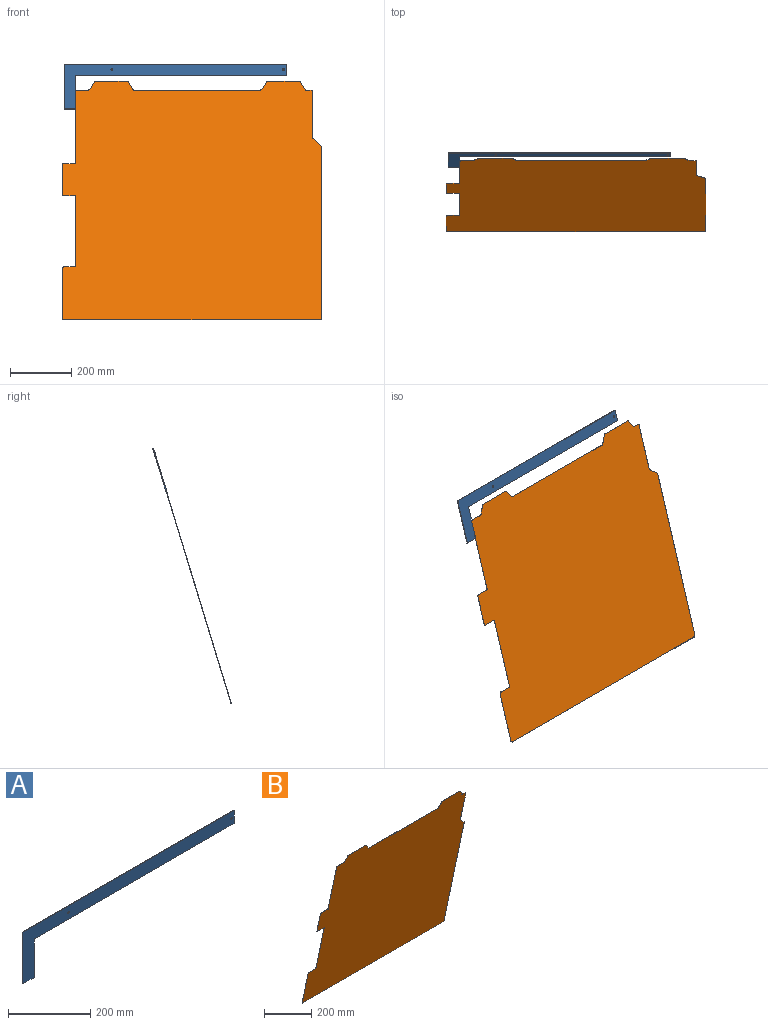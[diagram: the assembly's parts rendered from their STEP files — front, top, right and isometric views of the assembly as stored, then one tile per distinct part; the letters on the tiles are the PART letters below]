
ASSEMBLY  parts=2 mates=1
PART A: 10 faces, bbox 723.9x3.2x152.4 mm
  f0: plane 38.1x3.18mm, normal (1,0,0), area 121mm2, adj f1,f7,f8,f9
  f1: plane 723.9x3.18mm, normal (0,0,1), area 2298.4mm2, adj f0,f2,f8,f9
  f2: plane 152.4x3.18mm, normal (-1,0,0), area 483.9mm2, adj f1,f3,f8,f9
  f3: plane 38.1x3.18mm, normal (0,0,-1), area 121mm2, adj f2,f4,f8,f9
  f4: plane 114.3x3.18mm, normal (1,0,0), area 362.9mm2, adj f3,f7,f8,f9
  f5: cylinder r=3.17mm len=6.35mm, axis (0,1,0), area 63.3mm2, adj f8,f9
  f6: cylinder r=3.17mm len=6.35mm, axis (0,1,0), area 63.3mm2, adj f8,f9
  f7: plane 685.8x3.18mm, normal (0,0,-1), area 2177.4mm2, adj f0,f4,f8,f9
  f8: plane 723.9x152.4mm, normal (0,-1,0), area 31872.1mm2, adj f0,f1,f2,f3,f4,f5,f6,f7
  f9: plane 723.9x152.4mm, normal (0,1,0), area 31872.1mm2, adj f0,f1,f2,f3,f4,f5,f6,f7
PART B: 42 faces, bbox 845.6x169.3x794.4 mm
  f0: plane 845.62x794.26mm, normal (0,0.98,0.21), area 641403.5mm2, adj f1,f2,f3,f4,f5,f6,f7,f8
  f1: cylinder r=1mm len=1.08mm, axis (0,0.98,0.21), area 0.8mm2, adj f0,f2,f40,f41
  f2: plane 38.7x0.5mm, normal (0,0.21,-0.98), area 19.7mm2, adj f0,f1,f3,f41
  f3: cylinder r=5mm len=5mm, axis (0,0.98,0.21), area 4mm2, adj f0,f2,f4,f41
  f4: plane 97.82x21.27mm, normal (-1,0,0), area 50.7mm2, adj f0,f3,f5,f41
  f5: cylinder r=5mm len=5mm, axis (0,0.98,0.21), area 4mm2, adj f0,f4,f6,f41
  f6: plane 38.7x0.5mm, normal (0,-0.21,0.98), area 19.7mm2, adj f0,f5,f7,f41
  f7: cylinder r=1mm len=1.08mm, axis (0,0.98,0.21), area 0.8mm2, adj f0,f6,f8,f41
  f8: plane 239.07x51.29mm, normal (-1,0,0), area 124.1mm2, adj f0,f7,f9,f41
  f9: cylinder r=5mm len=5mm, axis (0,0.98,0.21), area 4mm2, adj f0,f8,f10,f41
  f10: plane 36.06x0.5mm, normal (0,-0.21,0.98), area 18.3mm2, adj f0,f9,f11,f41
  f11: cylinder r=5mm len=4.33mm, axis (0,0.98,0.21), area 2.7mm2, adj f0,f10,f12,f41
  f12: plane 24.56x14.43mm, normal (-0.87,-0.1,0.49), area 14.7mm2, adj f0,f11,f13,f41
  f13: cylinder r=5mm len=4.33mm, axis (0,0.98,0.21), area 2.7mm2, adj f0,f12,f14,f41
  f14: plane 103.09x0.5mm, normal (0,-0.21,0.98), area 52.4mm2, adj f0,f13,f15,f41
  f15: cylinder r=5mm len=4.33mm, axis (0,0.98,0.21), area 2.7mm2, adj f0,f14,f16,f41
  f16: plane 24.56x14.43mm, normal (0.87,-0.1,0.49), area 14.7mm2, adj f0,f15,f17,f41
  f17: cylinder r=5mm len=4.33mm, axis (0,0.98,0.21), area 2.7mm2, adj f0,f16,f18,f41
  f18: plane 410.72x0.5mm, normal (0,-0.21,0.98), area 208.6mm2, adj f0,f17,f19,f41
  f19: cylinder r=5mm len=4.33mm, axis (0,0.98,0.21), area 2.7mm2, adj f0,f18,f20,f41
  f20: plane 24.56x14.43mm, normal (-0.87,-0.1,0.49), area 14.7mm2, adj f0,f19,f21,f41
  f21: cylinder r=5mm len=4.33mm, axis (0,0.98,0.21), area 2.7mm2, adj f0,f20,f22,f41
  f22: plane 103.09x0.5mm, normal (0,-0.21,0.98), area 52.4mm2, adj f0,f21,f23,f41
  f23: cylinder r=5mm len=4.33mm, axis (0,0.98,0.21), area 2.7mm2, adj f0,f22,f24,f41
  f24: plane 24.56x14.43mm, normal (0.87,-0.1,0.49), area 14.7mm2, adj f0,f23,f25,f41
  f25: cylinder r=5mm len=4.33mm, axis (0,0.98,0.21), area 2.7mm2, adj f0,f24,f26,f41
  f26: plane 15.36x0.5mm, normal (0,-0.21,0.98), area 7.8mm2, adj f0,f25,f27,f41
  f27: cylinder r=5mm len=5mm, axis (0,0.98,0.21), area 4mm2, adj f0,f26,f28,f41
  f28: plane 153.67x33.14mm, normal (1,0,0), area 79.8mm2, adj f0,f27,f29,f41
  f29: cylinder r=5mm len=3.56mm, axis (0,0.98,0.21), area 2mm2, adj f0,f28,f30,f41
  f30: plane 27.29x26.8mm, normal (0.71,-0.15,0.69), area 19.6mm2, adj f0,f29,f31,f41
  f31: cylinder r=5mm len=3.56mm, axis (0,0.98,0.21), area 2mm2, adj f0,f30,f32,f41
  f32: plane 568.06x121.22mm, normal (1,0,0), area 295mm2, adj f0,f31,f33,f41
  f33: cylinder r=5mm len=5mm, axis (0,0.98,0.21), area 4mm2, adj f0,f32,f34,f41
  f34: plane 835.62x0.5mm, normal (0,0.21,-0.98), area 424.5mm2, adj f0,f33,f35,f41
  f35: cylinder r=5mm len=5mm, axis (0,0.98,0.21), area 4mm2, adj f0,f34,f36,f41
  f36: plane 166.59x35.88mm, normal (-1,0,0), area 86.5mm2, adj f0,f35,f37,f41
  f37: cylinder r=5mm len=5mm, axis (0,0.98,0.21), area 4mm2, adj f0,f36,f38,f41
  f38: plane 38.7x0.5mm, normal (0,-0.21,0.98), area 19.7mm2, adj f0,f37,f39,f41
  f39: cylinder r=1mm len=1.08mm, axis (0,0.98,0.21), area 0.8mm2, adj f0,f38,f40,f41
  f40: plane 234.47x50.31mm, normal (-1,0,0), area 121.7mm2, adj f0,f1,f39,f41
  f41: plane 845.62x794.26mm, normal (0,-0.98,-0.21), area 641403.5mm2, adj f1,f2,f3,f4,f5,f6,f7,f8
PLACE A rot(axis=(-1,0,0),17deg) t=(-197.35,-83.34,-54.52)mm
PLACE B rot(axis=(-1,0,0),29deg) t=(-100.62,-92.81,-1007.62)mm
MATE parallel B.f41 <-> A.f8  axis (0,-0.96,0.29) through (-107.71,-217.06,-485.36)mm
